# Revit family: DC_Rheem_PLM_Raypak_B0430ID
name_source: partatom
category: Mechanical Equipment
revit_build: Autodesk Revit 2017 (Build: 20160225_1515(x64)
units: mm (PartAtom-declared; Revit-internal decimal feet)

## family parameters
Cut with Voids When Loaded = No
Host = Face
Part Type = Normal
Room Calculation Point = No
Round Connector Dimension = Use Radius
Shared = No

## types (4) — shared parameters
BoxHeight_ANZRS = 985 mm  [stored 3.23163 ft]
ColdWaterConnectionDistance_ANZRS = 215 mm
ColdWaterInletDiameter_ANZRS = 40 mm
ColdWaterInletRadius_ANZRS = 20 mm  [stored 0.0656168 ft]
ConnectionHeight_ANZRS = 700 mm  [stored 2.29659 ft]
FootingOffsetRight_ANZRS = 105 mm
FootingOffset_ANZRS = 30 mm  [stored 0.0984252 ft]
FootingWidth_ANZRS = 50 mm  [stored 0.164042 ft]
GasConnectionDistance_ANZRS = 105 mm
GasInletHeight_ANZRS = 370 mm  [stored 1.21391 ft]
Height_ANZRS = 1805 mm  [stored 5.92192 ft]
HotWaterConnectionDistance_ANZRS = 170 mm
HotWaterOutletDiameter_ANZRS = 40 mm
HotWaterOutletRadius_ANZRS = 20 mm  [stored 0.0656168 ft]
Length_ANZRS = 675 mm  [stored 2.21457 ft]
LipHeight_ANZRS = 935 mm
Manufacturer = Raypak
PRVDiameter_ANZRS = 30 mm  [stored 0.0984252 ft]
PRVDistance_ANZRS = 210 mm  [stored 0.688976 ft]
PRVRadius_ANZRS = 15 mm  [stored 0.0492126 ft]
Stainless Steel = Raypak - Grey Powder Coated Steel
TopFuleDiameter_ANZRS = 255 mm  [stored 0.836614 ft]
URL = http://www.rheem.com.au
Width_ANZRS = 745 mm  [stored 2.44423 ft]
zero-valued in all types: Default Elevation

## per-type parameters (varying)
| type | Description | GasInletDiameter_ANZRS | GasInletRadius_ANZRS | Model | Type Comments |
| Raypak - Gas Water Heater- Indoor - 420 MJ/h  Natural gas, modulating gas control | Raypak - Gas Water Heater- Indoor - 420 MJ/h  Natural gas, modulating gas control | 25 mm  [stored 0.082021 ft] | 13 mm | B0430NCM/ID | Recovery 1610L/h @ 50oC rise |
| Raypak - Gas Water Heater- Indoor - 420  MJ/h  Natural gas, On/Off gas control | Raypak - Gas Water Heater- Indoor - 420  MJ/h  Natural gas, On/Off gas control | 20 mm  [stored 0.0656168 ft] | 10 mm  [stored 0.0328084 ft] | B0430NCO/ID | Recovery 1610L/h @ 50oC rise |
| Raypak - Gas Water Heater- Indoor - 396 MJ/h  Propane gas, modulating gas control | Raypak - Gas Water Heater- Indoor - 396 MJ/h  Propane gas, modulating gas control | 20 mm  [stored 0.0656168 ft] | 10 mm  [stored 0.0328084 ft] | B0430PCM/ID | Recovery 1514L/h @ 50oC rise |
| Raypak - Gas Water Heater- Indoor - 396 MJ/h  Propane gas, On/Off gas control | Raypak - Gas Water Heater- Indoor - 396 MJ/h  Propane gas, modulating gas control | 20 mm  [stored 0.0656168 ft] | 10 mm  [stored 0.0328084 ft] | B0350PCO/ID | Recovery 1514L/h @ 50oC rise |

note: [stored X ft] marks values corroborated as IEEE doubles in the binary element streams (Revit-internal decimal feet)

## geometry (parser evidence)
native form markers: Blend x6, Sweep x2
no freeform markers — native parametric forms only
